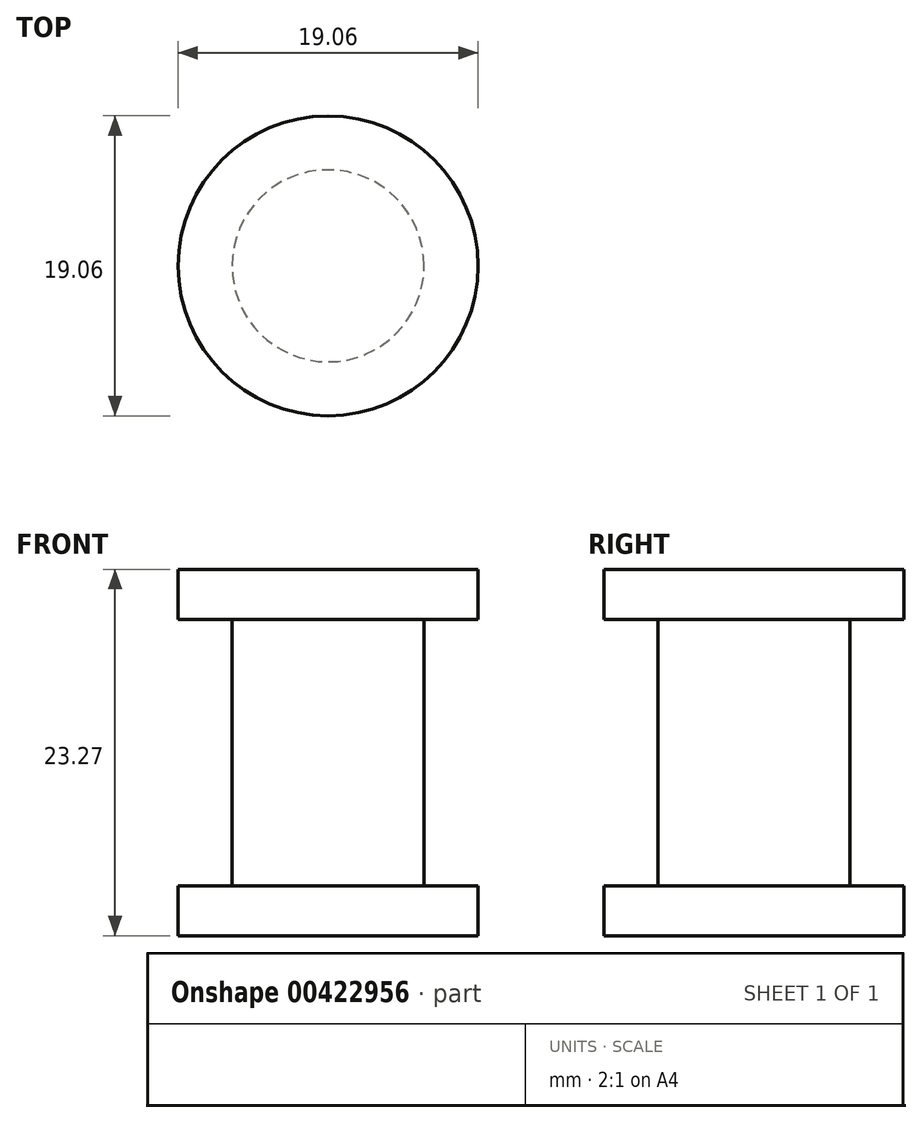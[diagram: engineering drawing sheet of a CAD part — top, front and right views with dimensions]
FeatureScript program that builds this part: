
annotation { "Feature Type Name" : "Feature", "Feature Type Description" : "" }
export const myFeature = defineFeature(function(context is Context, id is Id, definition is map)
    precondition{}
    {
        {
            var Q0;
            Q0=qCreatedBy(makeId("Top.planeOp"),FACE);
            var sketch = newSketch(context, id + "F0", { "sketchPlane" : qUnion([Q0])});
            skCircle(sketch, "E0", {"center": v(0, 0) * mm, "radius": 6.1 * mm});
            skSolve(sketch);
        }
        {
            var Q0;
            Q0=qSketchRegion(id+"F0",true);
            extrude(context, id + "F1", {"entities" : qUnion([Q0]), "depth" : 16.92 * mm, "offsetDistance" : 25.4 * mm});
        }
        {
            var Q0;
            Q0=makeQuery(id+"F1.opExtrude","CAP_FACE",FACE,{"disambiguationData":[OSD([sQuery(id+"F0.wireOp",EDGE,"E0")])],"isStart":false});
            var sketch = newSketch(context, id + "F2", { "sketchPlane" : qUnion([Q0])});
            skCircle(sketch, "E1", {"center": v(0, 0) * mm, "radius": 9.53 * mm});
            skSolve(sketch);
        }
        {
            var Q0;
            Q0=makeQuery(id+"F2.imprint","IMPRINT",FACE,{"disambiguationData":[TD([[makeQuery(id+"F2.imprint","IMPRINT",EDGE,{"derivedFrom":makeQuery(id+"F1.opExtrude","CAP_EDGE",EDGE,{"disambiguationData":[OSD([sQuery(id+"F0.wireOp",EDGE,"E0")])],"isStart":false})}),1.0]])]});
            var Q1;
            Q1=makeQuery(id+"F2.imprint","IMPRINT",FACE,{"disambiguationData":[TD([[makeQuery(id+"F2.imprint","IMPRINT",EDGE,{"derivedFrom":sQuery(id+"F2.wireOp",EDGE,"72a8668e-1708-4b08-b3c5-57bafb51af52")}),1.0]])]});
            var Q2;
            Q2=makeQuery(id+"F2.imprint","IMPRINT",FACE,{"disambiguationData":[TD([[makeQuery(id+"F2.imprint","IMPRINT",EDGE,{"derivedFrom":sQuery(id+"F2.wireOp",EDGE,"E1")}),1.0]])]});
            extrude(context, id + "F3", {"entities" : qUnion([Q0, Q1, Q2]), "operationType" : NewBodyOperationType.ADD, "depth" : 3.17 * mm, "offsetDistance" : 25.4 * mm});
        }
        {
            var Q0;
            Q0=makeQuery(id+"F1.opExtrude","CAP_FACE",FACE,{"disambiguationData":[OSD([sQuery(id+"F0.wireOp",EDGE,"E0")])],"isStart":true});
            var sketch = newSketch(context, id + "F4", { "sketchPlane" : qUnion([Q0])});
            skCircle(sketch, "E2", {"center": v(0, 0) * mm, "radius": 9.53 * mm});
            skSolve(sketch);
        }
        {
            var Q0;
            Q0 = qSketchRegion(id + "F4", true);
            extrude(context, id + "F5", {"entities" : qUnion([Q0]), "operationType" : NewBodyOperationType.ADD, "depth" : 3.17 * mm, "offsetDistance" : 25.4 * mm});
        }
    });
